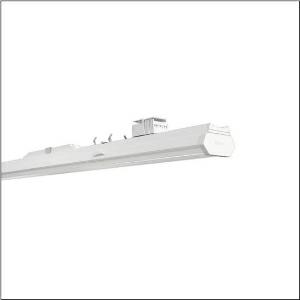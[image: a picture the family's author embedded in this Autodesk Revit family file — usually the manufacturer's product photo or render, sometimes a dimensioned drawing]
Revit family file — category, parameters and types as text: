
# Revit family: licross_21_protected_ho_52td11cn4c5s
name_source: partatom
category: Lighting Fixtures
units: mm (PartAtom-declared; Revit-internal decimal feet)

## family parameters
Cut with Voids When Loaded = No
Host = Face
Light Source = No
Part Type = Normal
Room Calculation Point = No
Round Connector Dimension = Use Diameter
Shared = No

## types (1)
- --- (1 x LED, 12650 lm, 68.9 W, 4000K)
    Apparent Load = 69 VA
    CIE Flux Codes = 84 94 98 99 100
    Color Rendering = 80
    Color Temperature = 4000K
    Default Elevation = 1800 mm
    Description = Licross 21 Protected HO, luminaire insert, of sheet steel, galvanised, coil coated, white, length: 1.500mm, width: 66mm, height: 67mm, LED rated luminous flux: 12.650lm, light colour: 840, SDCM (Standard Deviation of Colour Matching)MacAdam ≤ 3 SDCM (initial), control gear: ON/OFF Multilumen, CLOi, with plug, 3-pole, with phase selection, mains connection: 220..240V, AC, 50/60Hz, start of lifetime: 69W, end of service life: 83W, internal wiring halogen-free, primary light control with lens, of plastic, primary optical cover: cover, of PMMA, light emission: direct distribution, primary light characteristic: symmetric, protection rating (complete): IP54, insulation class (complete): insulation class I (protective earthing), certification: CE, ENEC, VDE, UKCA, protection symbol: D if used in an environment with non-conductive dust loads with corresponding accessories, impact resistance: IK06, permissible ambient temperature for indoor applications: -35..+35°C, corresponds to IFS (International Featured Standards) requirements for safety and quality in the food industry, reducing of maximum allowable ambient temperature of 5°C with ceiling mounting, LABS conformity tested according to VDMA 24364:2018-05, The light source and the operating device comply with the requirements of the Ecodesign Regulation (EU) 2019/2020 and are replaceable in accordance with this regulation, packaging unit: 1 piece
    Height = 92 mm
    Lamp = 1 x LED
    Lamp Light Flux = 12650 lm
    Lamp Power = 68.9 W
    Lamp count = 1
    Length = 1500 mm
    Luminous efficacy = 184 lm/W
    Manufacturer = Siteco
    ModVariant = No
    Model = 52TD11CN4C5S
    Mounting Place = Ceiling
    Mounting Type = Pendant
    Number of Poles = 1
    OnlyDefault = Yes
    Power Factor = 1
    Product Name = Licross 21 Protected HO
    Product group = luminaire insert | ceiling pendant
    ProductGroupID = 901
    Protection Class = Protection class I
    Protection Degree = IP 54
    RLX_Detail_Level = 1
    RLX_Emergency_Light_Flux = 0 lm
    RLX_Emergency_Type = 0
    RLX_Emergency_Type_DB = No
    RlxData = <blob elided: 22293 chars, md5=3343ff15>
    Socket = socket
    Standby Power = 0 W
    System Light Flux = 12650 lm
    System Power = 69 W
    Type Comments = factory setting: luminous flux: 100 % | (A | C | E) | 162 mA
    Type Image = l_1256148.jpg
    URL = http://relux.com
    VarID = @adj_110857
    Voltage = 0 V
    Weight = 0.00 kg
    Width = 88 mm

## geometry (parser evidence)
native form markers: Blend x4, Sweep x12
no freeform markers — native parametric forms only
